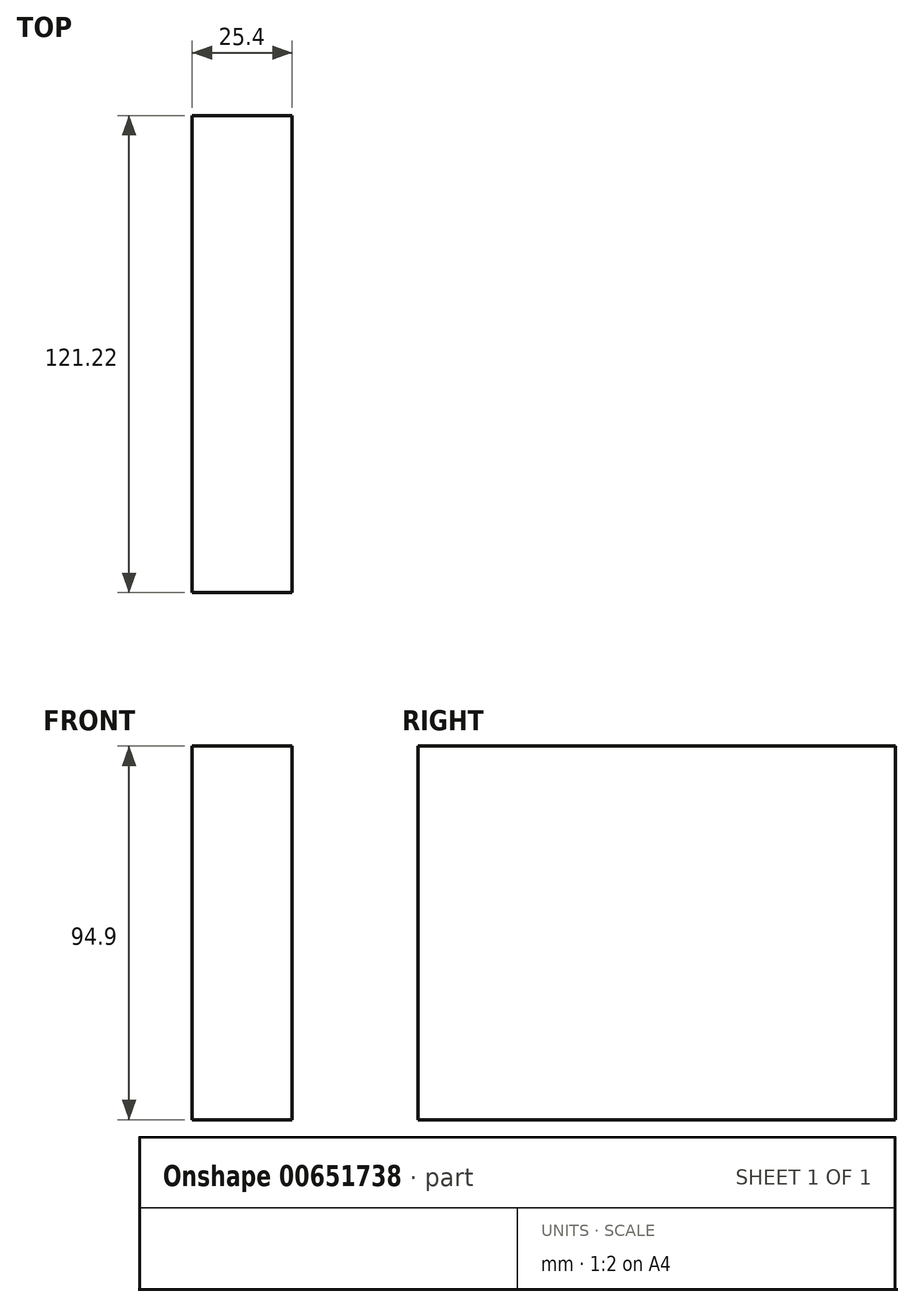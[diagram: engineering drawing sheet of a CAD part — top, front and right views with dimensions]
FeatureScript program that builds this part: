
annotation { "Feature Type Name" : "Feature", "Feature Type Description" : "" }
export const myFeature = defineFeature(function(context is Context, id is Id, definition is map)
    precondition{}
    {
        {
            var Q0;
            Q0=qCreatedBy(makeId("Right.planeOp"),FACE);
            var sketch = newSketch(context, id + "F0", { "sketchPlane" : qUnion([Q0])});
            skLineSegment(sketch, "E0.bottom", {"start": v(-43.64, 22.52) * mm, "end": v(77.58, 22.52) * mm});
            skLineSegment(sketch, "E0.top", {"start": v(-43.64, -72.38) * mm, "end": v(77.58, -72.38) * mm});
            skLineSegment(sketch, "E0.left", {"start": v(-43.64, 22.52) * mm, "end": v(-43.64, -72.38) * mm});
            skLineSegment(sketch, "E0.right", {"start": v(77.58, 22.52) * mm, "end": v(77.58, -72.38) * mm});
            skSolve(sketch);
        }
        {
            var Q0;
            Q0 = qSketchRegion(id + "F0", true);
            extrude(context, id + "F1", {"entities" : qUnion([Q0]), "depth" : 25.4 * mm, "offsetDistance" : 25.4 * mm});
        }
    });
